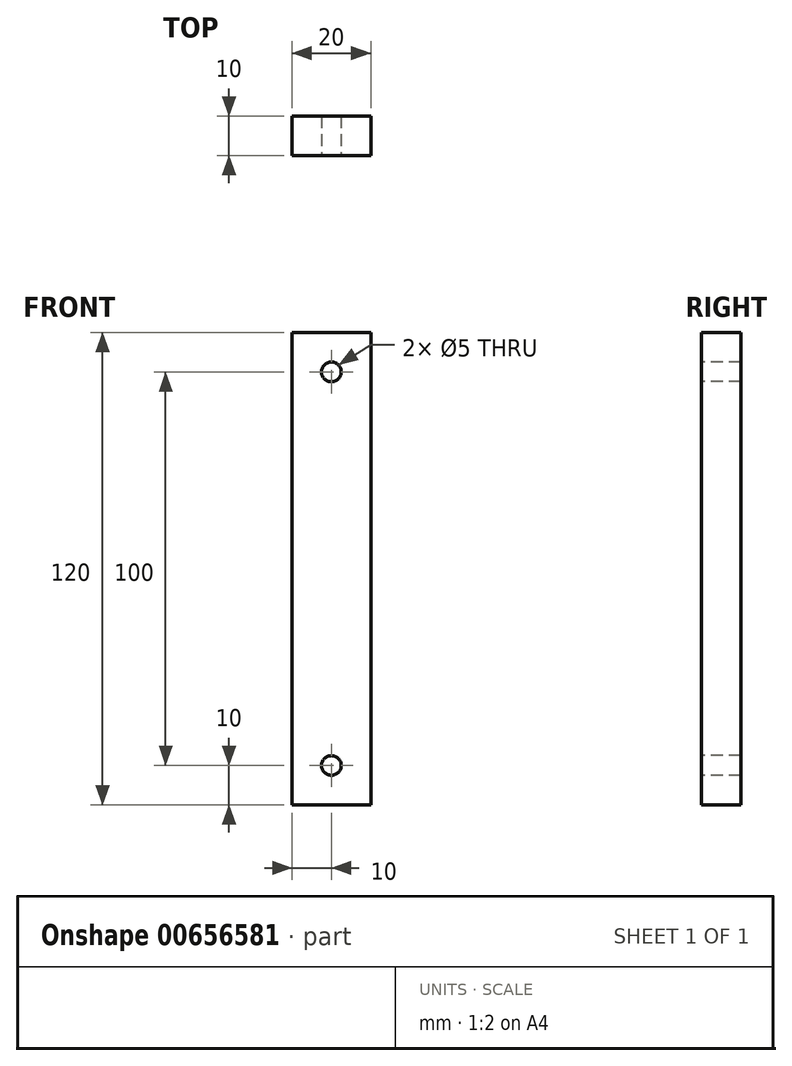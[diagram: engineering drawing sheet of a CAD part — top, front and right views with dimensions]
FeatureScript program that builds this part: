
annotation { "Feature Type Name" : "Feature", "Feature Type Description" : "" }
export const myFeature = defineFeature(function(context is Context, id is Id, definition is map)
    precondition{}
    {
        {
            var Q0;
            Q0=qCreatedBy(makeId("Front.planeOp"),FACE);
            var sketch = newSketch(context, id + "F0", { "sketchPlane" : qUnion([Q0])});
            skLineSegment(sketch, "E0.bottom", {"start": v(0, 0) * mm, "end": v(20, 0) * mm});
            skLineSegment(sketch, "E0.top", {"start": v(0, 120) * mm, "end": v(20, 120) * mm});
            skLineSegment(sketch, "E0.left", {"start": v(0, 0) * mm, "end": v(0, 120) * mm});
            skLineSegment(sketch, "E0.right", {"start": v(20, 0) * mm, "end": v(20, 120) * mm});
            skSolve(sketch);
        }
        {
            var Q0;
            Q0 = qSketchRegion(id + "F0", true);
            extrude(context, id + "F1", {"entities" : qUnion([Q0]), "depth" : 10 * mm, "offsetDistance" : 25 * mm});
        }
        {
            var Q0;
            Q0=makeQuery(id+"F1.opExtrude","CAP_FACE",FACE,{"disambiguationData":[OSD([sQuery(id+"F0.wireOp",EDGE,"E0.bottom"),sQuery(id+"F0.wireOp",EDGE,"E0.top"),sQuery(id+"F0.wireOp",EDGE,"E0.left"),sQuery(id+"F0.wireOp",EDGE,"E0.right")])],"isStart":false});
            var sketch = newSketch(context, id + "F2", { "sketchPlane" : qUnion([Q0])});
            skPoint(sketch, "E1", {"position": v(10, 110) * mm});
            skPoint(sketch, "E2", {"position": v(10, 10) * mm});
            skSolve(sketch);
        }
        {
            var Q0;
            Q0=sQuery(id+"F2.wireOp",VERTEX,"E1");
            var Q1;
            Q1=sQuery(id+"F2.wireOp",VERTEX,"E2");
            var Q2;
            Q2=makeQuery(id+"F1.opExtrude","SWEPT_BODY",BODY,{"disambiguationData":[OSD([sQuery(id+"F0.wireOp",EDGE,"E0.bottom"),sQuery(id+"F0.wireOp",EDGE,"E0.top"),sQuery(id+"F0.wireOp",EDGE,"E0.left"),sQuery(id+"F0.wireOp",EDGE,"E0.right")])]});
            hole(context, id + "F3", {"style" : HoleStyle.SIMPLE, "endStyle" : HoleEndStyle.THROUGH, "holeDiameter" : 5 * mm, "majorDiameter" : 5 * mm, "isTappedThrough" : true, "tappedDepth" : 12 * mm, "tapClearance" : 3, "locations" : qUnion([Q0, Q1]), "scope" : qUnion([Q2])});
        }
    });
